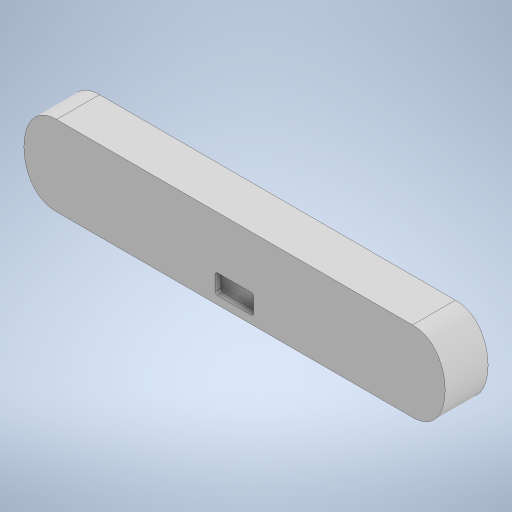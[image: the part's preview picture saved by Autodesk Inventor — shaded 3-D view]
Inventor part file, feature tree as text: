
AUTODESK INVENTOR PART (.ipt)
format: ipt  version: 2023 (Build 270158000, 158)  size: 3,336,192 bytes
history: native  units: in
note: dims shown in document units (in); Inventor stores cm internally (conversion verified against a paired STEP export)
features: extrude x4, other x1
ambient origin geometry x8: Origin, YZ Plane, XZ Plane, XY Plane, X Axis, Y Axis, Z Axis, Center Point
bodies: Solid1 (feature_tree)
feature tree (5):
  extrude  "Extrusion1"  Depth=0.3937in
  extrude  "Extrusion2"  Depth=2.3622in
  extrude  "Extrusion3"  Depth=0.3051in
  extrude  "Extrusion6"  Depth=0.3051in
  other  "Image3"
